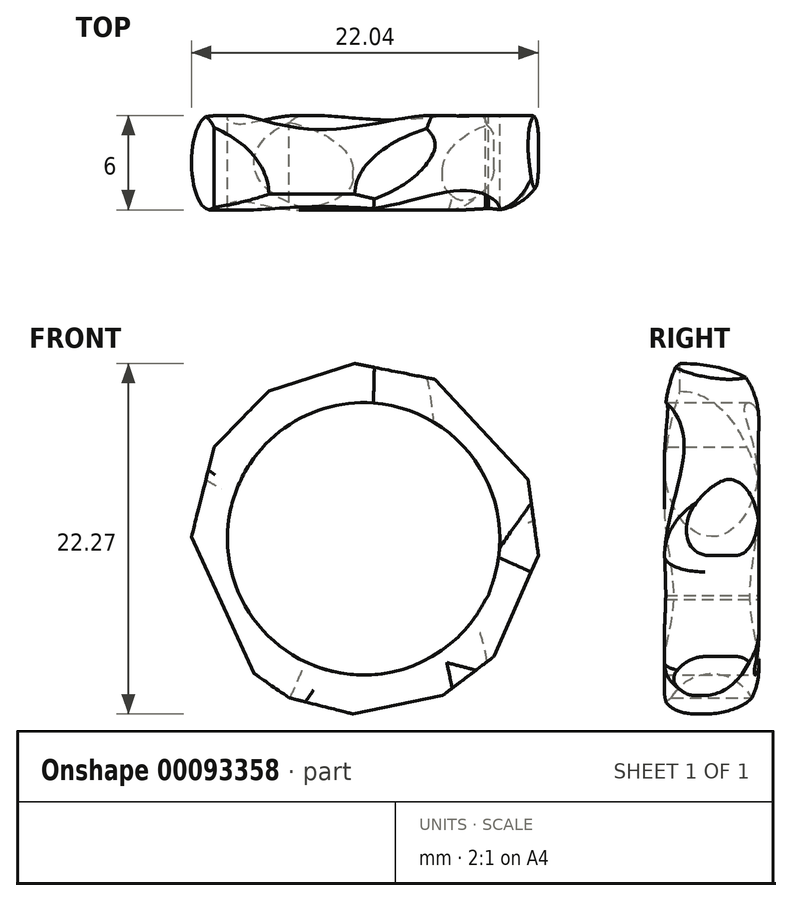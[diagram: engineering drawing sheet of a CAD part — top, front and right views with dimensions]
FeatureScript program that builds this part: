
annotation { "Feature Type Name" : "Feature", "Feature Type Description" : "" }
export const myFeature = defineFeature(function(context is Context, id is Id, definition is map)
    precondition{}
    {
        {
            var Q0;
            Q0=qCreatedBy(makeId("Front.planeOp"),FACE);
            var sketch = newSketch(context, id + "F0", { "sketchPlane" : qUnion([Q0])});
            skCircle(sketch, "E0", {"center": v(0, 0) * mm, "radius": 8.65 * mm});
            skCircle(sketch, "E1.0", {"center": v(0, 0) * mm, "radius": 11.15 * mm});
            skLineSegment(sketch, "E2", {"start": v(4.75, 10.09) * mm, "end": v(10.41, 3.99) * mm});
            skLineSegment(sketch, "E3", {"start": v(10.41, 3.99) * mm, "end": v(11.1, -1.06) * mm});
            skLineSegment(sketch, "E4", {"start": v(11.1, -1.06) * mm, "end": v(8.27, -7.48) * mm});
            skLineSegment(sketch, "E5", {"start": v(8.27, -7.48) * mm, "end": v(5, -9.96) * mm});
            skLineSegment(sketch, "E6", {"start": v(5, -9.96) * mm, "end": v(-0.66, -11.13) * mm});
            skLineSegment(sketch, "E7", {"start": v(-0.66, -11.13) * mm, "end": v(-4.73, -10.1) * mm});
            skLineSegment(sketch, "E8", {"start": v(-4.73, -10.1) * mm, "end": v(-7.78, -7.99) * mm});
            skLineSegment(sketch, "E9", {"start": v(-7.78, -7.99) * mm, "end": v(-11.13, -0.65) * mm});
            skLineSegment(sketch, "E10", {"start": v(-11.13, -0.65) * mm, "end": v(-9.5, 5.84) * mm});
            skLineSegment(sketch, "E11", {"start": v(-9.5, 5.84) * mm, "end": v(-6.02, 9.38) * mm});
            skLineSegment(sketch, "E12", {"start": v(-6.02, 9.38) * mm, "end": v(-0.56, 11.14) * mm});
            skLineSegment(sketch, "E13", {"start": v(-0.56, 11.14) * mm, "end": v(4.75, 10.09) * mm});
            skLineSegment(sketch, "E14", {"start": v(4.75, 10.09) * mm, "end": v(6.22, 6.02) * mm});
            skLineSegment(sketch, "E15", {"start": v(6.22, 6.02) * mm, "end": v(10.41, 3.99) * mm});
            skLineSegment(sketch, "E16", {"start": v(10.41, 3.99) * mm, "end": v(7.92, -3.6) * mm});
            skLineSegment(sketch, "E17", {"start": v(7.92, -3.6) * mm, "end": v(3.26, -10.32) * mm});
            skLineSegment(sketch, "E18", {"start": v(3.26, -10.32) * mm, "end": v(-3.38, -7.96) * mm});
            skLineSegment(sketch, "E19", {"start": v(-3.38, -7.96) * mm, "end": v(-8.79, -5.79) * mm});
            skLineSegment(sketch, "E20", {"start": v(-8.79, -5.79) * mm, "end": v(-8.56, -1.27) * mm});
            skLineSegment(sketch, "E21", {"start": v(-8.56, -1.27) * mm, "end": v(-10.15, 3.24) * mm});
            skLineSegment(sketch, "E22", {"start": v(-10.15, 3.24) * mm, "end": v(-4, 7.66) * mm});
            skLineSegment(sketch, "E23", {"start": v(-4, 7.66) * mm, "end": v(-1.86, 10.72) * mm});
            skLineSegment(sketch, "E24", {"start": v(-1.86, 10.72) * mm, "end": v(2.32, 8.33) * mm});
            skSolve(sketch);
        }
        {
            var Q0;
            {var subQ0=sQuery(id+"F0.wireOp",EDGE,"E15");Q0=makeQuery(id+"F0.imprint","IMPRINT",FACE,{"disambiguationData":[TD([[makeQuery(id+"F0.imprint","IMPRINT",EDGE,{"derivedFrom":subQ0}),-1.0]])]});}
            var Q1;
            {var subQ0=sQuery(id+"F0.wireOp",EDGE,"E13");Q1=makeQuery(id+"F0.imprint","IMPRINT",FACE,{"disambiguationData":[TD([[makeQuery(id+"F0.imprint","IMPRINT",EDGE,{"derivedFrom":subQ0}),-1.0]])]});}
            var Q2;
            {var subQ0=sQuery(id+"F0.wireOp",EDGE,"E23");Q2=makeQuery(id+"F0.imprint","IMPRINT",FACE,{"disambiguationData":[TD([[makeQuery(id+"F0.imprint","IMPRINT",EDGE,{"derivedFrom":subQ0}),-1.0]])]});}
            var Q3;
            {var subQ1=sQuery(id+"F0.wireOp",EDGE,"E11");Q3=makeQuery(id+"F0.imprint","IMPRINT",FACE,{"disambiguationData":[TD([[makeQuery(id+"F0.imprint","IMPRINT",EDGE,{"derivedFrom":subQ1}),-1.0]])]});}
            var Q4;
            {var subQ0=sQuery(id+"F0.wireOp",EDGE,"E21");Q4=makeQuery(id+"F0.imprint","IMPRINT",FACE,{"disambiguationData":[TD([[makeQuery(id+"F0.imprint","IMPRINT",EDGE,{"derivedFrom":subQ0}),-1.0]])]});}
            var Q5;
            {var subQ3=sQuery(id+"F0.wireOp",EDGE,"E20");Q5=makeQuery(id+"F0.imprint","IMPRINT",FACE,{"disambiguationData":[TD([[makeQuery(id+"F0.imprint","IMPRINT",EDGE,{"derivedFrom":subQ3}),1.0]])]});}
            var Q6;
            {var subQ0=sQuery(id+"F0.wireOp",EDGE,"E19");Q6=makeQuery(id+"F0.imprint","IMPRINT",FACE,{"disambiguationData":[TD([[makeQuery(id+"F0.imprint","IMPRINT",EDGE,{"derivedFrom":subQ0}),-1.0]])]});}
            var Q7;
            {var subQ2=sQuery(id+"F0.wireOp",EDGE,"E7");Q7=makeQuery(id+"F0.imprint","IMPRINT",FACE,{"disambiguationData":[TD([[makeQuery(id+"F0.imprint","IMPRINT",EDGE,{"derivedFrom":subQ2}),-1.0]])]});}
            var Q8;
            {var subQ0=sQuery(id+"F0.wireOp",EDGE,"E18");var subQ1=sQuery(id+"F0.wireOp",EDGE,"E0");var subQ2=makeQuery(id+"F0.imprint","INTERSECT",VERTEX,{"derivedFrom":[subQ1,subQ0]});Q8=makeQuery(id+"F0.imprint","IMPRINT",FACE,{"disambiguationData":[TD([[makeQuery(id+"F0.imprint","IMPRINT",EDGE,{"disambiguationData":[TD([[subQ2,-1.0]])],"derivedFrom":subQ1}),-1.0]])]});}
            var Q9;
            {var subQ7=sQuery(id+"F0.wireOp",EDGE,"E3");Q9=makeQuery(id+"F0.imprint","IMPRINT",FACE,{"disambiguationData":[TD([[makeQuery(id+"F0.imprint","IMPRINT",EDGE,{"derivedFrom":subQ7}),-1.0]])]});}
            var Q10;
            Q10=makeQuery(id+"F0.imprint","IMPRINT",FACE,{"disambiguationData":[TD([[makeQuery(id+"F0.imprint","IMPRINT",EDGE,{"derivedFrom":sQuery(id+"F0.wireOp",EDGE,"E2")}),-1.0]])]});
            extrude(context, id + "F1", {"entities" : qUnion([Q0, Q1, Q2, Q3, Q4, Q5, Q6, Q7, Q8, Q9, Q10]), "offsetDistance" : 25 * mm, "depth" : 3 * mm, "hasSecondDirection" : true, "secondDirectionOppositeDirection" : true, "secondDirectionDepth" : 3 * mm});
        }
        {
            var Q0;
            Q0=makeQuery(id+"F1.opExtrude","CAP_EDGE",EDGE,{"disambiguationData":[OSD([sQuery(id+"F0.wireOp",EDGE,"E2")])],"isStart":false});
            fillet(context, id + "F2", {"entities" : qUnion([Q0]), "radius" : 5 * mm, "tangentPropagation" : true, "allowEdgeOverflow" : false});
        }
        {
            var Q0;
            Q0=makeQuery(id+"F1.opExtrude","CAP_EDGE",EDGE,{"disambiguationData":[OSD([sQuery(id+"F0.wireOp",EDGE,"E4")])],"isStart":true});
            fillet(context, id + "F3", {"entities" : qUnion([Q0]), "radius" : 1.45 * mm, "tangentPropagation" : true, "allowEdgeOverflow" : false});
        }
        {
            var Q0;
            Q0=makeQuery(id+"F1.opExtrude","CAP_EDGE",EDGE,{"disambiguationData":[OSD([sQuery(id+"F0.wireOp",EDGE,"E4")])],"isStart":false});
            fillet(context, id + "F4", {"entities" : qUnion([Q0]), "radius" : 2.58 * mm, "tangentPropagation" : true, "allowEdgeOverflow" : false});
        }
        {
            var Q0;
            Q0=makeQuery(id+"F1.opExtrude","CAP_EDGE",EDGE,{"disambiguationData":[OSD([sQuery(id+"F0.wireOp",EDGE,"E2")])],"isStart":true});
            fillet(context, id + "F5", {"entities" : qUnion([Q0]), "radius" : 1.89 * mm, "tangentPropagation" : true, "allowEdgeOverflow" : false});
        }
        {
            var Q0;
            Q0=makeQuery(id+"F1.opExtrude","CAP_EDGE",EDGE,{"disambiguationData":[OSD([sQuery(id+"F0.wireOp",EDGE,"E12")])],"isStart":true});
            fillet(context, id + "F6", {"entities" : qUnion([Q0]), "radius" : 5 * mm, "tangentPropagation" : true, "allowEdgeOverflow" : false});
        }
        {
            var Q0;
            Q0=makeQuery(id+"F1.opExtrude","CAP_EDGE",EDGE,{"disambiguationData":[OSD([sQuery(id+"F0.wireOp",EDGE,"E12")])],"isStart":false});
            fillet(context, id + "F7", {"entities" : qUnion([Q0]), "radius" : 8.63 * mm, "tangentPropagation" : true, "allowEdgeOverflow" : false});
        }
        {
            var Q0;
            Q0=makeQuery(id+"F1.opExtrude","CAP_EDGE",EDGE,{"disambiguationData":[OSD([sQuery(id+"F0.wireOp",EDGE,"E9")])],"isStart":false});
            var Q1;
            Q1=makeQuery(id+"F1.opExtrude","CAP_EDGE",EDGE,{"disambiguationData":[OSD([sQuery(id+"F0.wireOp",EDGE,"E6")])],"isStart":true});
            fillet(context, id + "F8", {"entities" : qUnion([Q0, Q1]), "radius" : 3.5 * mm, "tangentPropagation" : true, "allowEdgeOverflow" : false});
        }
        {
            var Q0;
            Q0=makeQuery(id+"F1.opExtrude","CAP_EDGE",EDGE,{"disambiguationData":[OSD([sQuery(id+"F0.wireOp",EDGE,"E9")])],"isStart":true});
            fillet(context, id + "F9", {"entities" : qUnion([Q0]), "radius" : 3 * mm, "tangentPropagation" : true, "allowEdgeOverflow" : false});
        }
        {
            var Q0;
            Q0=makeQuery(id+"F1.opExtrude","CAP_EDGE",EDGE,{"disambiguationData":[OSD([sQuery(id+"F0.wireOp",EDGE,"E6")])],"isStart":false});
            fillet(context, id + "F10", {"entities" : qUnion([Q0]), "radius" : 2 * mm, "tangentPropagation" : true, "allowEdgeOverflow" : false});
        }
    });
